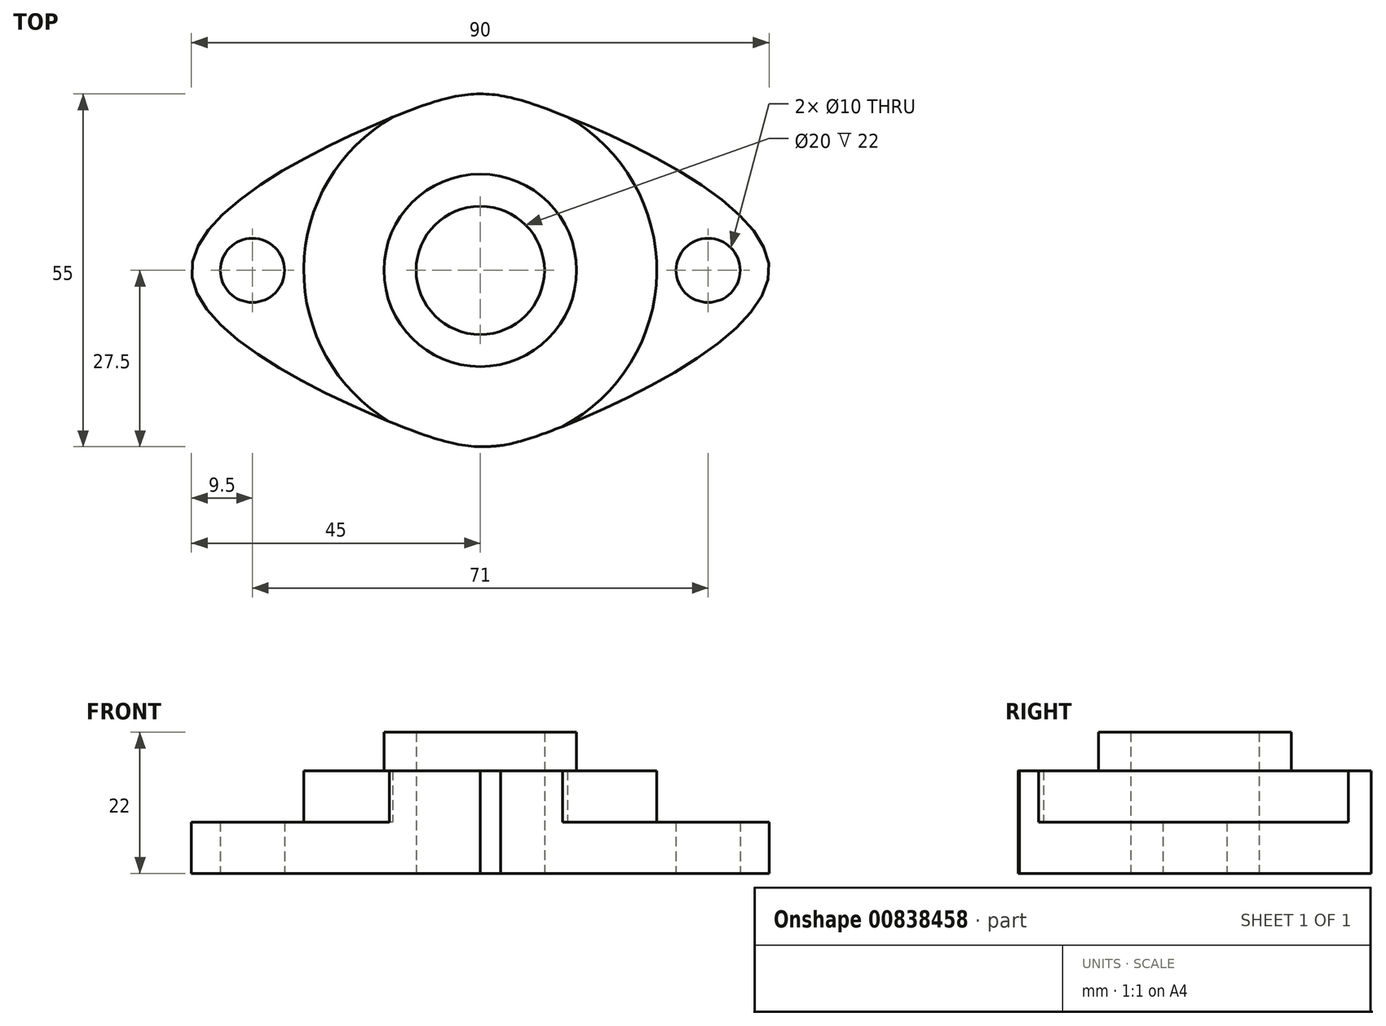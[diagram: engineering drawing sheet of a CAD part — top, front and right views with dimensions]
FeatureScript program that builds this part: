
annotation { "Feature Type Name" : "Feature", "Feature Type Description" : "" }
export const myFeature = defineFeature(function(context is Context, id is Id, definition is map)
    precondition{}
    {
        {
            var Q0;
            Q0=qCreatedBy(makeId("Top.planeOp"),FACE);
            var sketch = newSketch(context, id + "F0", { "sketchPlane" : qUnion([Q0])});
            skLineSegment(sketch, "E0", {"start": v(-35.5, 0) * mm, "end": v(35.5, 0) * mm, "construction": true});
            skCircle(sketch, "E1", {"center": v(0, 0) * mm, "radius": 10 * mm});
            skCircle(sketch, "E2", {"center": v(-35.5, 0) * mm, "radius": 5 * mm});
            skCircle(sketch, "E3", {"center": v(35.5, 0) * mm, "radius": 5 * mm});
            skLineSegment(sketch, "E4", {"start": v(0, -27.5) * mm, "end": v(0, 27.5) * mm, "construction": true});
            skFitSpline(sketch, "E5", {"points": [v(0, 27.5) * mm, v(-13.63, 23.88) * mm, v(-45, 0) * mm, v(-14.13, -23.6) * mm, v(0, -27.5) * mm, v(12.8, -24.34) * mm, v(45, 0) * mm, v(13.61, 23.9) * mm, v(0, 27.5) * mm]});
            skCircle(sketch, "E6", {"center": v(0, 0) * mm, "radius": 27.5 * mm});
            skCircle(sketch, "E7", {"center": v(0, 0) * mm, "radius": 15 * mm});
            skSolve(sketch);
        }
        {
            var Q0;
            Q0=makeQuery(id+"F0.imprint","IMPRINT",FACE,{"disambiguationData":[TD([[makeQuery(id+"F0.imprint","IMPRINT",EDGE,{"derivedFrom":sQuery(id+"F0.wireOp",EDGE,"E2")}),-1.0]])]});
            var Q1;
            Q1=makeQuery(id+"F0.imprint","IMPRINT",FACE,{"disambiguationData":[TD([[makeQuery(id+"F0.imprint","IMPRINT",EDGE,{"derivedFrom":sQuery(id+"F0.wireOp",EDGE,"E3")}),-1.0]])]});
            extrude(context, id + "F1", {"entities" : qUnion([Q0, Q1]), "depth" : 8 * mm, "offsetDistance" : 25 * mm});
        }
        {
            var Q0;
            Q0=makeQuery(id+"F0.imprint","IMPRINT",FACE,{"disambiguationData":[TD([[makeQuery(id+"F0.imprint","IMPRINT",EDGE,{"derivedFrom":sQuery(id+"F0.wireOp",EDGE,"E7")}),-1.0]])]});
            extrude(context, id + "F2", {"entities" : qUnion([Q0]), "operationType" : NewBodyOperationType.ADD, "depth" : 16 * mm, "offsetDistance" : 25 * mm});
        }
        {
            var Q0;
            Q0=makeQuery(id+"F0.imprint","IMPRINT",FACE,{"disambiguationData":[TD([[makeQuery(id+"F0.imprint","IMPRINT",EDGE,{"derivedFrom":sQuery(id+"F0.wireOp",EDGE,"E1")}),-1.0]])]});
            extrude(context, id + "F3", {"entities" : qUnion([Q0]), "operationType" : NewBodyOperationType.ADD, "depth" : 22 * mm, "offsetDistance" : 25 * mm});
        }
    });
